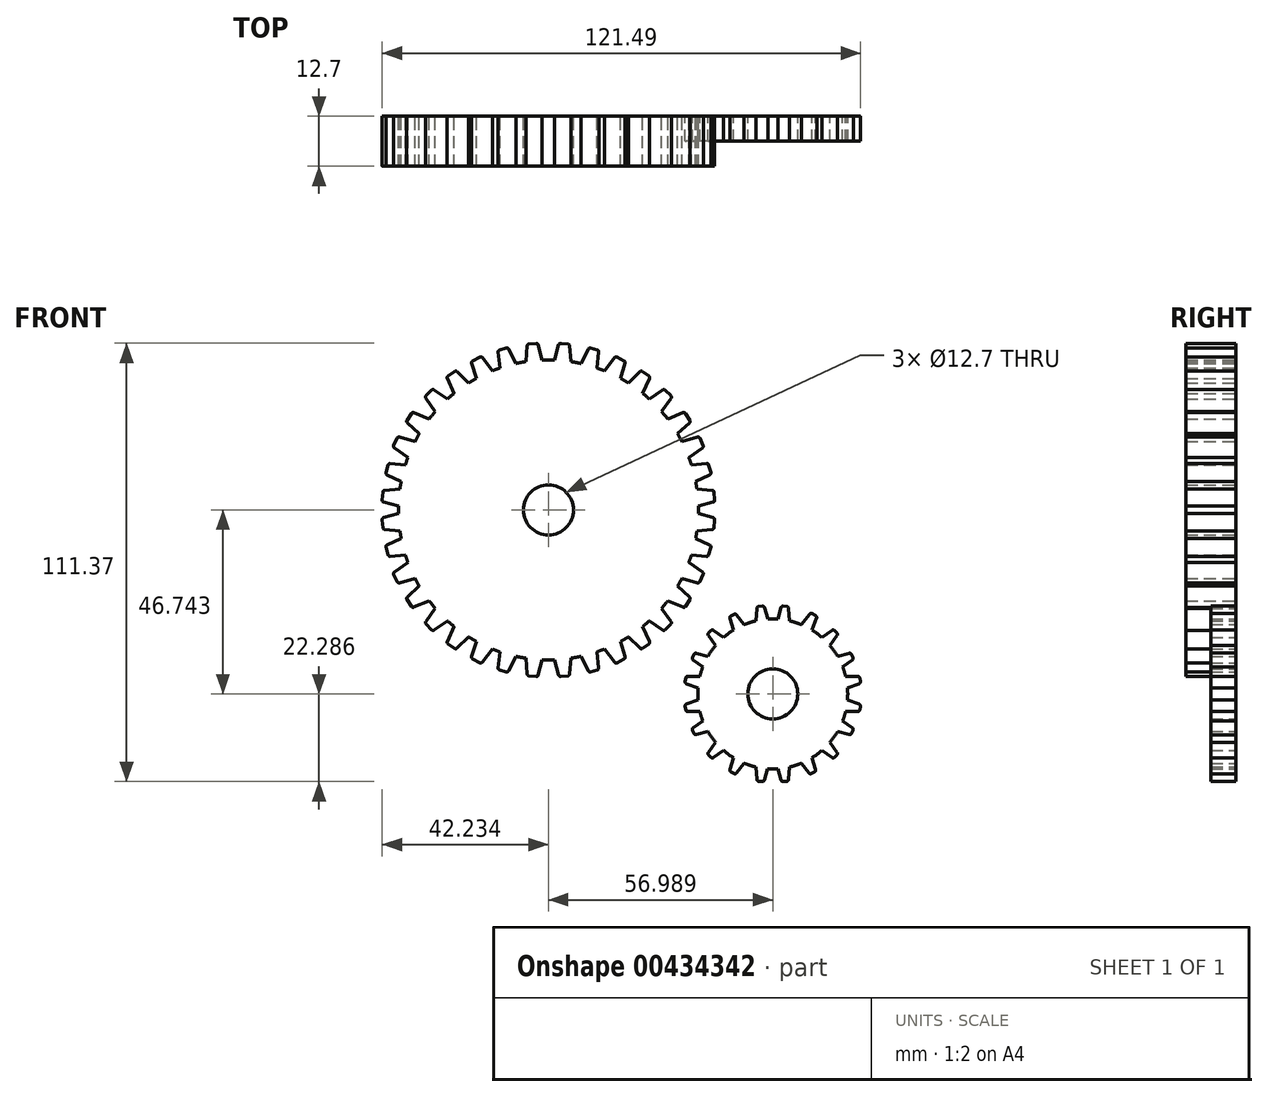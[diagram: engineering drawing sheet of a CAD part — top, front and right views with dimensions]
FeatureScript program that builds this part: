
annotation { "Feature Type Name" : "Feature", "Feature Type Description" : "" }
export const myFeature = defineFeature(function(context is Context, id is Id, definition is map)
    precondition{}
    {
        {
            var Q0;
            Q0=qCreatedBy(makeId("Front.planeOp"),FACE);
            var sketch = newSketch(context, id + "F0", { "sketchPlane" : qUnion([Q0])});
            skCircle(sketch, "E0", {"center": v(-12.13, 9.66) * mm, "radius": 38.1 * mm});
            skCircle(sketch, "E1", {"center": v(-12.13, 9.66) * mm, "radius": 6.35 * mm});
            skLineSegment(sketch, "E2", {"start": v(-6.7, 44.55) * mm, "end": v(-10.75, 44.9) * mm});
            skLineSegment(sketch, "E3", {"start": v(-11.15, 45.49) * mm, "end": v(-9.51, 51.62) * mm});
            skLineSegment(sketch, "E4", {"start": v(-8.98, 52) * mm, "end": v(-7.2, 51.84) * mm});
            skLineSegment(sketch, "E5", {"start": v(-6.75, 51.38) * mm, "end": v(-6.2, 45.05) * mm});
            skPoint(sketch, "E6.visualSharp", {"position": v(-6.78, 51.8) * mm});
            skPoint(sketch, "E7.visualSharp", {"position": v(-9.4, 52.03) * mm});
            skArc(sketch, "E7.filletArc", {"start": v(-8.98, 52) * mm, "mid": v(-9.31, 51.9) * mm, "end": v(-9.51, 51.62) * mm});
            skPoint(sketch, "E8.visualSharp", {"position": v(-6.15, 44.5) * mm});
            skArc(sketch, "E8.filletArc", {"start": v(-6.7, 44.55) * mm, "mid": v(-6.33, 44.68) * mm, "end": v(-6.2, 45.05) * mm});
            skPoint(sketch, "E9.visualSharp", {"position": v(-11.3, 44.95) * mm});
            skArc(sketch, "E9.filletArc", {"start": v(-11.15, 45.49) * mm, "mid": v(-11.09, 45.1) * mm, "end": v(-10.75, 44.9) * mm});
            skArc(sketch, "E10.filletArc", {"start": v(-6.75, 51.38) * mm, "mid": v(-6.9, 51.7) * mm, "end": v(-7.2, 51.84) * mm});
            skLineSegment(sketch, "E11", {"start": v(-12.13, -28.44) * mm, "end": v(-12.13, 47.76) * mm, "construction": true});
            skLineSegment(sketch, "E12", {"start": v(-50.23, 9.66) * mm, "end": v(25.97, 9.66) * mm, "construction": true});
            skLineSegment(sketch, "E13", {"start": v(-0.73, 43.06) * mm, "end": v(-4.62, 44.26) * mm});
            skLineSegment(sketch, "E14", {"start": v(-4.9, 44.92) * mm, "end": v(-2, 50.57) * mm});
            skLineSegment(sketch, "E15", {"start": v(-1.4, 50.82) * mm, "end": v(0.3, 50.3) * mm});
            skLineSegment(sketch, "E16", {"start": v(0.66, 49.75) * mm, "end": v(-0.13, 43.45) * mm});
            skPoint(sketch, "E17.visualSharp", {"position": v(1, 48.98) * mm});
            skPoint(sketch, "E18.visualSharp", {"position": v(-1.8, 50.94) * mm});
            skArc(sketch, "E18.filletArc", {"start": v(-1.4, 50.82) * mm, "mid": v(-1.74, 50.8) * mm, "end": v(-2, 50.57) * mm});
            skPoint(sketch, "E19.visualSharp", {"position": v(-0.2, 42.9) * mm});
            skArc(sketch, "E19.filletArc", {"start": v(-0.73, 43.06) * mm, "mid": v(-0.34, 43.11) * mm, "end": v(-0.13, 43.45) * mm});
            skPoint(sketch, "E20.visualSharp", {"position": v(-5.14, 44.42) * mm});
            skArc(sketch, "E20.filletArc", {"start": v(-4.9, 44.92) * mm, "mid": v(-4.9, 44.52) * mm, "end": v(-4.62, 44.26) * mm});
            skArc(sketch, "E21.filletArc", {"start": v(0.66, 49.75) * mm, "mid": v(0.58, 50.09) * mm, "end": v(0.3, 50.3) * mm});
            skLineSegment(sketch, "E22", {"start": v(4.8, 40.61) * mm, "end": v(0.96, 42.6) * mm});
            skLineSegment(sketch, "E23", {"start": v(0.8, 43.3) * mm, "end": v(4.66, 48.34) * mm});
            skLineSegment(sketch, "E24", {"start": v(5.3, 48.48) * mm, "end": v(7.1, 47.55) * mm});
            skLineSegment(sketch, "E25", {"start": v(7.36, 46.94) * mm, "end": v(5.45, 40.88) * mm});
            skPoint(sketch, "E26.visualSharp", {"position": v(7.48, 47.35) * mm});
            skPoint(sketch, "E27.visualSharp", {"position": v(4.92, 48.68) * mm});
            skArc(sketch, "E27.filletArc", {"start": v(5.3, 48.48) * mm, "mid": v(4.96, 48.53) * mm, "end": v(4.66, 48.34) * mm});
            skPoint(sketch, "E28.visualSharp", {"position": v(5.29, 40.36) * mm});
            skArc(sketch, "E28.filletArc", {"start": v(4.8, 40.61) * mm, "mid": v(5.19, 40.6) * mm, "end": v(5.45, 40.88) * mm});
            skPoint(sketch, "E29.visualSharp", {"position": v(0.47, 42.86) * mm});
            skArc(sketch, "E29.filletArc", {"start": v(0.8, 43.3) * mm, "mid": v(0.72, 42.91) * mm, "end": v(0.96, 42.6) * mm});
            skArc(sketch, "E30.filletArc", {"start": v(7.36, 46.94) * mm, "mid": v(7.34, 47.3) * mm, "end": v(7.1, 47.55) * mm});
            skLineSegment(sketch, "E31", {"start": v(10.2, 37.1) * mm, "end": v(6.65, 39.59) * mm});
            skLineSegment(sketch, "E32", {"start": v(6.59, 40.3) * mm, "end": v(11.08, 44.78) * mm});
            skLineSegment(sketch, "E33", {"start": v(11.73, 44.84) * mm, "end": v(13.4, 43.67) * mm});
            skLineSegment(sketch, "E34", {"start": v(13.56, 43.04) * mm, "end": v(10.88, 37.29) * mm});
            skPoint(sketch, "E35.visualSharp", {"position": v(13.74, 43.43) * mm});
            skPoint(sketch, "E36.visualSharp", {"position": v(11.38, 45.08) * mm});
            skArc(sketch, "E36.filletArc", {"start": v(11.73, 44.84) * mm, "mid": v(11.4, 44.93) * mm, "end": v(11.08, 44.78) * mm});
            skPoint(sketch, "E37.visualSharp", {"position": v(10.64, 36.79) * mm});
            skArc(sketch, "E37.filletArc", {"start": v(10.2, 37.1) * mm, "mid": v(10.58, 37.04) * mm, "end": v(10.88, 37.29) * mm});
            skPoint(sketch, "E38.visualSharp", {"position": v(6.2, 39.9) * mm});
            skArc(sketch, "E38.filletArc", {"start": v(6.59, 40.3) * mm, "mid": v(6.45, 39.92) * mm, "end": v(6.65, 39.59) * mm});
            skArc(sketch, "E39.filletArc", {"start": v(13.56, 43.04) * mm, "mid": v(13.6, 43.39) * mm, "end": v(13.4, 43.67) * mm});
            skLineSegment(sketch, "E40", {"start": v(14.66, 32.76) * mm, "end": v(11.6, 35.83) * mm});
            skLineSegment(sketch, "E41", {"start": v(11.67, 36.54) * mm, "end": v(16.88, 40.17) * mm});
            skLineSegment(sketch, "E42", {"start": v(17.53, 40.1) * mm, "end": v(18.97, 38.67) * mm});
            skLineSegment(sketch, "E43", {"start": v(19.02, 38.02) * mm, "end": v(15.36, 32.82) * mm});
            skPoint(sketch, "E44.visualSharp", {"position": v(19.27, 38.36) * mm});
            skPoint(sketch, "E45.visualSharp", {"position": v(17.23, 40.41) * mm});
            skArc(sketch, "E45.filletArc", {"start": v(17.53, 40.1) * mm, "mid": v(17.22, 40.26) * mm, "end": v(16.88, 40.17) * mm});
            skPoint(sketch, "E46.visualSharp", {"position": v(15.05, 32.37) * mm});
            skArc(sketch, "E46.filletArc", {"start": v(14.66, 32.76) * mm, "mid": v(15.02, 32.63) * mm, "end": v(15.36, 32.82) * mm});
            skPoint(sketch, "E47.visualSharp", {"position": v(11.22, 36.22) * mm});
            skArc(sketch, "E47.filletArc", {"start": v(11.67, 36.54) * mm, "mid": v(11.47, 36.2) * mm, "end": v(11.6, 35.83) * mm});
            skArc(sketch, "E48.filletArc", {"start": v(19.02, 38.02) * mm, "mid": v(19.11, 38.35) * mm, "end": v(18.97, 38.67) * mm});
            skLineSegment(sketch, "E49", {"start": v(18.32, 27.6) * mm, "end": v(16, 31.25) * mm});
            skLineSegment(sketch, "E50", {"start": v(16.22, 31.92) * mm, "end": v(22.08, 34.35) * mm});
            skLineSegment(sketch, "E51", {"start": v(22.7, 34.15) * mm, "end": v(23.8, 32.44) * mm});
            skLineSegment(sketch, "E52", {"start": v(23.71, 31.8) * mm, "end": v(19.03, 27.5) * mm});
            skPoint(sketch, "E53.visualSharp", {"position": v(24.03, 32.08) * mm});
            skPoint(sketch, "E54.visualSharp", {"position": v(22.48, 34.51) * mm});
            skArc(sketch, "E54.filletArc", {"start": v(22.7, 34.15) * mm, "mid": v(22.43, 34.37) * mm, "end": v(22.08, 34.35) * mm});
            skPoint(sketch, "E55.visualSharp", {"position": v(18.62, 27.13) * mm});
            skArc(sketch, "E55.filletArc", {"start": v(18.32, 27.6) * mm, "mid": v(18.65, 27.39) * mm, "end": v(19.03, 27.5) * mm});
            skPoint(sketch, "E56.visualSharp", {"position": v(15.7, 31.71) * mm});
            skArc(sketch, "E56.filletArc", {"start": v(16.22, 31.92) * mm, "mid": v(15.95, 31.64) * mm, "end": v(16, 31.25) * mm});
            skArc(sketch, "E57.filletArc", {"start": v(23.71, 31.8) * mm, "mid": v(23.87, 32.1) * mm, "end": v(23.8, 32.44) * mm});
            skLineSegment(sketch, "E58", {"start": v(21.12, 21.96) * mm, "end": v(19.29, 25.88) * mm});
            skLineSegment(sketch, "E59", {"start": v(19.6, 26.52) * mm, "end": v(25.72, 28.16) * mm});
            skLineSegment(sketch, "E60", {"start": v(26.32, 27.89) * mm, "end": v(27.17, 26.04) * mm});
            skLineSegment(sketch, "E61", {"start": v(27, 25.41) * mm, "end": v(21.8, 21.77) * mm});
            skPoint(sketch, "E62.visualSharp", {"position": v(27.35, 25.66) * mm});
            skPoint(sketch, "E63.visualSharp", {"position": v(26.14, 28.27) * mm});
            skArc(sketch, "E63.filletArc", {"start": v(26.32, 27.89) * mm, "mid": v(26.07, 28.13) * mm, "end": v(25.72, 28.16) * mm});
            skPoint(sketch, "E64.visualSharp", {"position": v(21.35, 21.45) * mm});
            skArc(sketch, "E64.filletArc", {"start": v(21.12, 21.96) * mm, "mid": v(21.42, 21.7) * mm, "end": v(21.8, 21.77) * mm});
            skPoint(sketch, "E65.visualSharp", {"position": v(19.06, 26.38) * mm});
            skArc(sketch, "E65.filletArc", {"start": v(19.6, 26.52) * mm, "mid": v(19.29, 26.27) * mm, "end": v(19.29, 25.88) * mm});
            skArc(sketch, "E66.filletArc", {"start": v(27, 25.41) * mm, "mid": v(27.2, 25.7) * mm, "end": v(27.17, 26.04) * mm});
            skLineSegment(sketch, "E67", {"start": v(22.38, 16.38) * mm, "end": v(21.39, 20.06) * mm});
            skLineSegment(sketch, "E68", {"start": v(21.98, 20.92) * mm, "end": v(28.05, 21.46) * mm});
            skLineSegment(sketch, "E69", {"start": v(28.59, 21.08) * mm, "end": v(29.12, 19.12) * mm});
            skLineSegment(sketch, "E70", {"start": v(28.84, 18.53) * mm, "end": v(23.32, 15.95) * mm});
            skPoint(sketch, "E71.visualSharp", {"position": v(29.23, 18.71) * mm});
            skPoint(sketch, "E72.visualSharp", {"position": v(28.48, 21.5) * mm});
            skArc(sketch, "E72.filletArc", {"start": v(28.59, 21.08) * mm, "mid": v(28.39, 21.37) * mm, "end": v(28.05, 21.46) * mm});
            skPoint(sketch, "E73.visualSharp", {"position": v(22.6, 15.6) * mm});
            skArc(sketch, "E73.filletArc", {"start": v(22.38, 16.38) * mm, "mid": v(22.75, 15.95) * mm, "end": v(23.32, 15.95) * mm});
            skPoint(sketch, "E74.visualSharp", {"position": v(21.18, 20.85) * mm});
            skArc(sketch, "E74.filletArc", {"start": v(21.98, 20.92) * mm, "mid": v(21.49, 20.63) * mm, "end": v(21.39, 20.06) * mm});
            skArc(sketch, "E75.filletArc", {"start": v(28.84, 18.53) * mm, "mid": v(29.09, 18.78) * mm, "end": v(29.12, 19.12) * mm});
            skLineSegment(sketch, "E76", {"start": v(23, 10.65) * mm, "end": v(22.66, 14.45) * mm});
            skLineSegment(sketch, "E77", {"start": v(23.4, 15.18) * mm, "end": v(29.47, 14.65) * mm});
            skLineSegment(sketch, "E78", {"start": v(29.93, 14.19) * mm, "end": v(30.1, 12.17) * mm});
            skLineSegment(sketch, "E79", {"start": v(29.73, 11.63) * mm, "end": v(23.85, 10.05) * mm});
            skPoint(sketch, "E80.visualSharp", {"position": v(30.14, 11.74) * mm});
            skPoint(sketch, "E81.visualSharp", {"position": v(29.9, 14.61) * mm});
            skArc(sketch, "E81.filletArc", {"start": v(29.93, 14.19) * mm, "mid": v(29.78, 14.5) * mm, "end": v(29.47, 14.65) * mm});
            skPoint(sketch, "E82.visualSharp", {"position": v(23.06, 9.84) * mm});
            skArc(sketch, "E82.filletArc", {"start": v(23, 10.65) * mm, "mid": v(23.28, 10.15) * mm, "end": v(23.85, 10.05) * mm});
            skPoint(sketch, "E83.visualSharp", {"position": v(22.6, 15.25) * mm});
            skArc(sketch, "E83.filletArc", {"start": v(23.4, 15.18) * mm, "mid": v(22.86, 14.99) * mm, "end": v(22.66, 14.45) * mm});
            skArc(sketch, "E84.filletArc", {"start": v(29.73, 11.63) * mm, "mid": v(30.02, 11.83) * mm, "end": v(30.1, 12.17) * mm});
            skArc(sketch, "E85.MirrorCS", {"start": v(-24.9, 49.75) * mm, "mid": v(-24.83, 50.09) * mm, "end": v(-24.55, 50.3) * mm});
            skArc(sketch, "E86.MirrorCS", {"start": v(-47.96, 31.8) * mm, "mid": v(-48.12, 32.1) * mm, "end": v(-48.05, 32.44) * mm});
            skArc(sketch, "E87.MirrorCS", {"start": v(-37.81, 43.04) * mm, "mid": v(-37.84, 43.39) * mm, "end": v(-37.64, 43.67) * mm});
            skArc(sketch, "E88.MirrorCS", {"start": v(-43.27, 38.02) * mm, "mid": v(-43.36, 38.35) * mm, "end": v(-43.22, 38.67) * mm});
            skArc(sketch, "E89.MirrorCS", {"start": v(-31.6, 46.94) * mm, "mid": v(-31.6, 47.3) * mm, "end": v(-31.36, 47.55) * mm});
            skArc(sketch, "E90.MirrorCS", {"start": v(-19.36, 44.92) * mm, "mid": v(-19.34, 44.52) * mm, "end": v(-19.63, 44.26) * mm});
            skArc(sketch, "E91.MirrorCS", {"start": v(-53.98, 11.63) * mm, "mid": v(-54.27, 11.83) * mm, "end": v(-54.36, 12.17) * mm});
            skLineSegment(sketch, "E92.MirrorCS", {"start": v(-46.96, 34.15) * mm, "end": v(-48.05, 32.44) * mm});
            skLineSegment(sketch, "E93.MirrorCS", {"start": v(-35.98, 44.84) * mm, "end": v(-37.64, 43.67) * mm});
            skLineSegment(sketch, "E94.MirrorCS", {"start": v(-22.86, 50.82) * mm, "end": v(-24.55, 50.3) * mm});
            skArc(sketch, "E95.MirrorCS", {"start": v(-17.5, 51.38) * mm, "mid": v(-17.36, 51.7) * mm, "end": v(-17.04, 51.84) * mm});
            skLineSegment(sketch, "E96.MirrorCS", {"start": v(-41.78, 40.1) * mm, "end": v(-43.22, 38.67) * mm});
            skLineSegment(sketch, "E97.MirrorCS", {"start": v(-29.55, 48.48) * mm, "end": v(-31.36, 47.55) * mm});
            skArc(sketch, "E98.MirrorCS", {"start": v(-22.86, 50.82) * mm, "mid": v(-22.51, 50.8) * mm, "end": v(-22.26, 50.57) * mm});
            skArc(sketch, "E99.MirrorCS", {"start": v(-46.96, 34.15) * mm, "mid": v(-46.68, 34.37) * mm, "end": v(-46.34, 34.35) * mm});
            skArc(sketch, "E100.MirrorCS", {"start": v(-35.98, 44.84) * mm, "mid": v(-35.64, 44.93) * mm, "end": v(-35.33, 44.78) * mm});
            skArc(sketch, "E101.MirrorCS", {"start": v(-50.57, 27.89) * mm, "mid": v(-50.32, 28.13) * mm, "end": v(-49.97, 28.16) * mm});
            skArc(sketch, "E102.MirrorCS", {"start": v(-41.78, 40.1) * mm, "mid": v(-41.47, 40.26) * mm, "end": v(-41.13, 40.17) * mm});
            skArc(sketch, "E103.MirrorCS", {"start": v(-29.55, 48.48) * mm, "mid": v(-29.2, 48.53) * mm, "end": v(-28.92, 48.34) * mm});
            skArc(sketch, "E104.MirrorCS", {"start": v(-23.52, 43.06) * mm, "mid": v(-23.9, 43.11) * mm, "end": v(-24.12, 43.45) * mm});
            skArc(sketch, "E105.MirrorCS", {"start": v(-29.05, 40.61) * mm, "mid": v(-29.44, 40.6) * mm, "end": v(-29.7, 40.88) * mm});
            skArc(sketch, "E106.MirrorCS", {"start": v(-47.24, 10.65) * mm, "mid": v(-47.53, 10.15) * mm, "end": v(-48.1, 10.05) * mm});
            skArc(sketch, "E107.MirrorCS", {"start": v(-30.84, 40.3) * mm, "mid": v(-30.7, 39.92) * mm, "end": v(-30.9, 39.59) * mm});
            skArc(sketch, "E108.MirrorCS", {"start": v(-43.84, 26.52) * mm, "mid": v(-43.54, 26.27) * mm, "end": v(-43.54, 25.88) * mm});
            skArc(sketch, "E109.MirrorCS", {"start": v(-35.92, 36.54) * mm, "mid": v(-35.72, 36.2) * mm, "end": v(-35.86, 35.83) * mm});
            skArc(sketch, "E110.MirrorCS", {"start": v(-25.06, 43.3) * mm, "mid": v(-24.97, 42.91) * mm, "end": v(-25.21, 42.6) * mm});
            skArc(sketch, "E111.MirrorCS", {"start": v(-47.65, 15.18) * mm, "mid": v(-47.1, 14.99) * mm, "end": v(-46.91, 14.45) * mm});
            skArc(sketch, "E112.MirrorCS", {"start": v(-53.1, 18.53) * mm, "mid": v(-53.34, 18.78) * mm, "end": v(-53.37, 19.12) * mm});
            skArc(sketch, "E113.MirrorCS", {"start": v(-51.26, 25.41) * mm, "mid": v(-51.46, 25.7) * mm, "end": v(-51.43, 26.04) * mm});
            skLineSegment(sketch, "E114.MirrorCS", {"start": v(-52.84, 21.08) * mm, "end": v(-53.37, 19.12) * mm});
            skLineSegment(sketch, "E115.MirrorCS", {"start": v(-23.52, 43.06) * mm, "end": v(-19.63, 44.26) * mm});
            skLineSegment(sketch, "E116.MirrorCS", {"start": v(-17.56, 44.55) * mm, "end": v(-13.5, 44.9) * mm});
            skLineSegment(sketch, "E117.MirrorCS", {"start": v(-15.27, 52) * mm, "end": v(-17.04, 51.84) * mm});
            skArc(sketch, "E118.MirrorCS", {"start": v(-15.27, 52) * mm, "mid": v(-14.94, 51.9) * mm, "end": v(-14.74, 51.62) * mm});
            skArc(sketch, "E119.MirrorCS", {"start": v(-17.56, 44.55) * mm, "mid": v(-17.92, 44.68) * mm, "end": v(-18.06, 45.05) * mm});
            skArc(sketch, "E120.MirrorCS", {"start": v(-13.1, 45.49) * mm, "mid": v(-13.16, 45.1) * mm, "end": v(-13.5, 44.9) * mm});
            skLineSegment(sketch, "E121.MirrorCS", {"start": v(-50.57, 27.89) * mm, "end": v(-51.43, 26.04) * mm});
            skLineSegment(sketch, "E122.MirrorCS", {"start": v(-54.18, 14.19) * mm, "end": v(-54.36, 12.17) * mm});
            skArc(sketch, "E123.MirrorCS", {"start": v(-52.84, 21.08) * mm, "mid": v(-52.64, 21.37) * mm, "end": v(-52.3, 21.46) * mm});
            skArc(sketch, "E124.MirrorCS", {"start": v(-54.18, 14.19) * mm, "mid": v(-54.03, 14.5) * mm, "end": v(-53.72, 14.65) * mm});
            skArc(sketch, "E125.MirrorCS", {"start": v(-34.44, 37.1) * mm, "mid": v(-34.83, 37.04) * mm, "end": v(-35.13, 37.29) * mm});
            skLineSegment(sketch, "E126.MirrorCS", {"start": v(-42.58, 27.6) * mm, "end": v(-40.25, 31.25) * mm});
            skLineSegment(sketch, "E127.MirrorCS", {"start": v(-47.24, 10.65) * mm, "end": v(-46.91, 14.45) * mm});
            skLineSegment(sketch, "E128.MirrorCS", {"start": v(-45.37, 21.96) * mm, "end": v(-43.54, 25.88) * mm});
            skArc(sketch, "E129.MirrorCS", {"start": v(-46.63, 16.38) * mm, "mid": v(-47, 15.95) * mm, "end": v(-47.58, 15.95) * mm});
            skArc(sketch, "E130.MirrorCS", {"start": v(-42.58, 27.6) * mm, "mid": v(-42.9, 27.39) * mm, "end": v(-43.28, 27.5) * mm});
            skArc(sketch, "E131.MirrorCS", {"start": v(-38.9, 32.76) * mm, "mid": v(-39.27, 32.63) * mm, "end": v(-39.61, 32.82) * mm});
            skArc(sketch, "E132.MirrorCS", {"start": v(-45.37, 21.96) * mm, "mid": v(-45.67, 21.7) * mm, "end": v(-46.05, 21.77) * mm});
            skArc(sketch, "E133.MirrorCS", {"start": v(-46.24, 20.92) * mm, "mid": v(-45.74, 20.63) * mm, "end": v(-45.64, 20.06) * mm});
            skArc(sketch, "E134.MirrorCS", {"start": v(-40.47, 31.92) * mm, "mid": v(-40.2, 31.64) * mm, "end": v(-40.25, 31.25) * mm});
            skLineSegment(sketch, "E135.MirrorCS", {"start": v(-46.63, 16.38) * mm, "end": v(-45.64, 20.06) * mm});
            skLineSegment(sketch, "E136.MirrorCS", {"start": v(-34.44, 37.1) * mm, "end": v(-30.9, 39.59) * mm});
            skLineSegment(sketch, "E137.MirrorCS", {"start": v(-29.05, 40.61) * mm, "end": v(-25.21, 42.6) * mm});
            skLineSegment(sketch, "E138.MirrorCS", {"start": v(-38.9, 32.76) * mm, "end": v(-35.86, 35.83) * mm});
            skPoint(sketch, "E139.MirrorP", {"position": v(-48.28, 32.08) * mm});
            skPoint(sketch, "E140.MirrorP", {"position": v(-17.47, 51.8) * mm});
            skPoint(sketch, "E141.MirrorP", {"position": v(-53.48, 18.71) * mm});
            skPoint(sketch, "E142.MirrorP", {"position": v(-51.6, 25.66) * mm});
            skPoint(sketch, "E143.MirrorP", {"position": v(-43.52, 38.36) * mm});
            skPoint(sketch, "E144.MirrorP", {"position": v(-54.4, 11.74) * mm});
            skPoint(sketch, "E145.MirrorP", {"position": v(-25.24, 48.98) * mm});
            skPoint(sketch, "E146.MirrorP", {"position": v(-31.73, 47.35) * mm});
            skPoint(sketch, "E147.MirrorP", {"position": v(-38, 43.43) * mm});
            skPoint(sketch, "E148.MirrorP", {"position": v(-24.05, 42.9) * mm});
            skPoint(sketch, "E149.MirrorP", {"position": v(-35.63, 45.08) * mm});
            skPoint(sketch, "E150.MirrorP", {"position": v(-29.17, 48.68) * mm});
            skPoint(sketch, "E151.MirrorP", {"position": v(-46.84, 15.25) * mm});
            skPoint(sketch, "E152.MirrorP", {"position": v(-12.95, 44.95) * mm});
            skPoint(sketch, "E153.MirrorP", {"position": v(-45.43, 20.85) * mm});
            skPoint(sketch, "E154.MirrorP", {"position": v(-39.3, 32.37) * mm});
            skPoint(sketch, "E155.MirrorP", {"position": v(-46.73, 34.51) * mm});
            skPoint(sketch, "E156.MirrorP", {"position": v(-34.9, 36.79) * mm});
            skPoint(sketch, "E157.MirrorP", {"position": v(-24.72, 42.86) * mm});
            skPoint(sketch, "E158.MirrorP", {"position": v(-19.1, 44.42) * mm});
            skPoint(sketch, "E159.MirrorP", {"position": v(-50.39, 28.27) * mm});
            skLineSegment(sketch, "E160.MirrorCS", {"start": v(-46.24, 20.92) * mm, "end": v(-52.3, 21.46) * mm});
            skLineSegment(sketch, "E161.MirrorCS", {"start": v(-40.47, 31.92) * mm, "end": v(-46.34, 34.35) * mm});
            skLineSegment(sketch, "E162.MirrorCS", {"start": v(-30.84, 40.3) * mm, "end": v(-35.33, 44.78) * mm});
            skPoint(sketch, "E163.MirrorP", {"position": v(-29.54, 40.36) * mm});
            skPoint(sketch, "E164.MirrorP", {"position": v(-41.48, 40.41) * mm});
            skLineSegment(sketch, "E165.MirrorCS", {"start": v(-25.06, 43.3) * mm, "end": v(-28.92, 48.34) * mm});
            skLineSegment(sketch, "E166.MirrorCS", {"start": v(-47.65, 15.18) * mm, "end": v(-53.72, 14.65) * mm});
            skLineSegment(sketch, "E167.MirrorCS", {"start": v(-43.84, 26.52) * mm, "end": v(-49.97, 28.16) * mm});
            skLineSegment(sketch, "E168.MirrorCS", {"start": v(-35.92, 36.54) * mm, "end": v(-41.13, 40.17) * mm});
            skLineSegment(sketch, "E169.MirrorCS", {"start": v(-19.36, 44.92) * mm, "end": v(-22.26, 50.57) * mm});
            skLineSegment(sketch, "E170.MirrorCS", {"start": v(-13.1, 45.49) * mm, "end": v(-14.74, 51.62) * mm});
            skLineSegment(sketch, "E171.MirrorCS", {"start": v(-17.5, 51.38) * mm, "end": v(-18.06, 45.05) * mm});
            skPoint(sketch, "E172.MirrorP", {"position": v(-14.85, 52.03) * mm});
            skPoint(sketch, "E173.MirrorP", {"position": v(-52.73, 21.5) * mm});
            skPoint(sketch, "E174.MirrorP", {"position": v(-30.45, 39.9) * mm});
            skPoint(sketch, "E175.MirrorP", {"position": v(-42.87, 27.13) * mm});
            skPoint(sketch, "E176.MirrorP", {"position": v(-35.47, 36.22) * mm});
            skPoint(sketch, "E177.MirrorP", {"position": v(-54.14, 14.61) * mm});
            skPoint(sketch, "E178.MirrorP", {"position": v(-45.6, 21.45) * mm});
            skLineSegment(sketch, "E179.MirrorCS", {"start": v(-24.9, 49.75) * mm, "end": v(-24.12, 43.45) * mm});
            skLineSegment(sketch, "E180.MirrorCS", {"start": v(-53.1, 18.53) * mm, "end": v(-47.58, 15.95) * mm});
            skLineSegment(sketch, "E181.MirrorCS", {"start": v(-47.96, 31.8) * mm, "end": v(-43.28, 27.5) * mm});
            skLineSegment(sketch, "E182.MirrorCS", {"start": v(-37.81, 43.04) * mm, "end": v(-35.13, 37.29) * mm});
            skLineSegment(sketch, "E183.MirrorCS", {"start": v(-51.26, 25.41) * mm, "end": v(-46.05, 21.77) * mm});
            skLineSegment(sketch, "E184.MirrorCS", {"start": v(-43.27, 38.02) * mm, "end": v(-39.61, 32.82) * mm});
            skLineSegment(sketch, "E185.MirrorCS", {"start": v(-53.98, 11.63) * mm, "end": v(-48.1, 10.05) * mm});
            skLineSegment(sketch, "E186.MirrorCS", {"start": v(-31.6, 46.94) * mm, "end": v(-29.7, 40.88) * mm});
            skPoint(sketch, "E187.MirrorP", {"position": v(-22.45, 50.94) * mm});
            skPoint(sketch, "E188.MirrorP", {"position": v(-47.31, 9.84) * mm});
            skPoint(sketch, "E189.MirrorP", {"position": v(-43.3, 26.38) * mm});
            skPoint(sketch, "E190.MirrorP", {"position": v(-18.1, 44.5) * mm});
            skPoint(sketch, "E191.MirrorP", {"position": v(-46.84, 15.6) * mm});
            skPoint(sketch, "E192.MirrorP", {"position": v(-39.96, 31.71) * mm});
            skArc(sketch, "E193.MirrorCS", {"start": v(-17.5, -32.06) * mm, "mid": v(-17.36, -32.38) * mm, "end": v(-17.04, -32.52) * mm});
            skArc(sketch, "E194.MirrorCS", {"start": v(-35.92, -17.22) * mm, "mid": v(-35.72, -16.88) * mm, "end": v(-35.86, -16.51) * mm});
            skArc(sketch, "E195.MirrorCS", {"start": v(-34.44, -17.79) * mm, "mid": v(-34.83, -17.72) * mm, "end": v(-35.13, -17.97) * mm});
            skArc(sketch, "E196.MirrorCS", {"start": v(-54.18, 5.13) * mm, "mid": v(-54.03, 4.81) * mm, "end": v(-53.72, 4.67) * mm});
            skArc(sketch, "E197.MirrorCS", {"start": v(0.66, -30.43) * mm, "mid": v(0.58, -30.77) * mm, "end": v(0.3, -30.98) * mm});
            skArc(sketch, "E198.MirrorCS", {"start": v(-46.63, 2.93) * mm, "mid": v(-47, 3.37) * mm, "end": v(-47.58, 3.37) * mm});
            skArc(sketch, "E199.MirrorCS", {"start": v(-52.84, -1.77) * mm, "mid": v(-52.64, -2.05) * mm, "end": v(-52.3, -2.14) * mm});
            skArc(sketch, "E200.MirrorCS", {"start": v(-53.1, 0.79) * mm, "mid": v(-53.34, 0.54) * mm, "end": v(-53.37, 0.2) * mm});
            skLineSegment(sketch, "E201.MirrorCS", {"start": v(-47.65, 4.14) * mm, "end": v(-53.72, 4.67) * mm});
            skArc(sketch, "E202.MirrorCS", {"start": v(-47.65, 4.14) * mm, "mid": v(-47.1, 4.33) * mm, "end": v(-46.91, 4.87) * mm});
            skLineSegment(sketch, "E203.MirrorCS", {"start": v(5.3, -29.16) * mm, "end": v(7.1, -28.23) * mm});
            skLineSegment(sketch, "E204.MirrorCS", {"start": v(26.32, -8.57) * mm, "end": v(27.17, -6.73) * mm});
            skLineSegment(sketch, "E205.MirrorCS", {"start": v(0.8, -23.98) * mm, "end": v(4.66, -29.02) * mm});
            skArc(sketch, "E206.MirrorCS", {"start": v(23, 8.67) * mm, "mid": v(23.28, 9.16) * mm, "end": v(23.85, 9.26) * mm});
            skLineSegment(sketch, "E207.MirrorCS", {"start": v(-52.84, -1.77) * mm, "end": v(-53.37, 0.2) * mm});
            skArc(sketch, "E208.MirrorCS", {"start": v(21.12, -2.64) * mm, "mid": v(21.42, -2.39) * mm, "end": v(21.8, -2.45) * mm});
            skLineSegment(sketch, "E209.MirrorCS", {"start": v(21.12, -2.64) * mm, "end": v(19.29, -6.56) * mm});
            skLineSegment(sketch, "E210.MirrorCS", {"start": v(-35.98, -25.52) * mm, "end": v(-37.64, -24.36) * mm});
            skLineSegment(sketch, "E211.MirrorCS", {"start": v(-35.92, -17.22) * mm, "end": v(-41.13, -20.85) * mm});
            skArc(sketch, "E212.MirrorCS", {"start": v(13.56, -23.73) * mm, "mid": v(13.6, -24.07) * mm, "end": v(13.4, -24.36) * mm});
            skArc(sketch, "E213.MirrorCS", {"start": v(23.71, -12.47) * mm, "mid": v(23.87, -12.78) * mm, "end": v(23.8, -13.12) * mm});
            skArc(sketch, "E214.MirrorCS", {"start": v(28.84, 0.79) * mm, "mid": v(29.09, 0.54) * mm, "end": v(29.12, 0.2) * mm});
            skArc(sketch, "E215.MirrorCS", {"start": v(-51.26, -6.1) * mm, "mid": v(-51.46, -6.38) * mm, "end": v(-51.43, -6.73) * mm});
            skArc(sketch, "E216.MirrorCS", {"start": v(5.3, -29.16) * mm, "mid": v(4.96, -29.2) * mm, "end": v(4.66, -29.02) * mm});
            skArc(sketch, "E217.MirrorCS", {"start": v(26.32, -8.57) * mm, "mid": v(26.07, -8.81) * mm, "end": v(25.72, -8.84) * mm});
            skLineSegment(sketch, "E218.MirrorCS", {"start": v(-46.24, -1.6) * mm, "end": v(-52.3, -2.14) * mm});
            skArc(sketch, "E219.MirrorCS", {"start": v(21.98, -1.6) * mm, "mid": v(21.49, -1.31) * mm, "end": v(21.39, -0.75) * mm});
            skArc(sketch, "E220.MirrorCS", {"start": v(-53.98, 7.69) * mm, "mid": v(-54.27, 7.49) * mm, "end": v(-54.36, 7.15) * mm});
            skArc(sketch, "E221.MirrorCS", {"start": v(-4.9, -25.6) * mm, "mid": v(-4.9, -25.2) * mm, "end": v(-4.62, -24.94) * mm});
            skLineSegment(sketch, "E222.MirrorCS", {"start": v(29.73, 7.69) * mm, "end": v(23.85, 9.26) * mm});
            skLineSegment(sketch, "E223.MirrorCS", {"start": v(-41.78, -20.8) * mm, "end": v(-43.22, -19.35) * mm});
            skLineSegment(sketch, "E224.MirrorCS", {"start": v(27, -6.1) * mm, "end": v(21.8, -2.45) * mm});
            skArc(sketch, "E225.MirrorCS", {"start": v(-19.36, -25.6) * mm, "mid": v(-19.34, -25.2) * mm, "end": v(-19.63, -24.94) * mm});
            skLineSegment(sketch, "E226.MirrorCS", {"start": v(-54.18, 5.13) * mm, "end": v(-54.36, 7.15) * mm});
            skArc(sketch, "E227.MirrorCS", {"start": v(27, -6.1) * mm, "mid": v(27.2, -6.38) * mm, "end": v(27.17, -6.73) * mm});
            skLineSegment(sketch, "E228.MirrorCS", {"start": v(28.59, -1.77) * mm, "end": v(29.12, 0.2) * mm});
            skLineSegment(sketch, "E229.MirrorCS", {"start": v(11.73, -25.52) * mm, "end": v(13.4, -24.36) * mm});
            skLineSegment(sketch, "E230.MirrorCS", {"start": v(0.66, -30.43) * mm, "end": v(-0.13, -24.13) * mm});
            skLineSegment(sketch, "E231.MirrorCS", {"start": v(-34.44, -17.79) * mm, "end": v(-30.9, -20.27) * mm});
            skArc(sketch, "E232.MirrorCS", {"start": v(-0.73, -23.74) * mm, "mid": v(-0.34, -23.8) * mm, "end": v(-0.13, -24.13) * mm});
            skArc(sketch, "E233.MirrorCS", {"start": v(-1.4, -31.5) * mm, "mid": v(-1.74, -31.48) * mm, "end": v(-2, -31.25) * mm});
            skArc(sketch, "E234.MirrorCS", {"start": v(11.73, -25.52) * mm, "mid": v(11.4, -25.61) * mm, "end": v(11.08, -25.47) * mm});
            skLineSegment(sketch, "E235.MirrorCS", {"start": v(-23.52, -23.74) * mm, "end": v(-19.63, -24.94) * mm});
            skArc(sketch, "E236.MirrorCS", {"start": v(0.8, -23.98) * mm, "mid": v(0.72, -23.6) * mm, "end": v(0.96, -23.29) * mm});
            skLineSegment(sketch, "E237.MirrorCS", {"start": v(-15.27, -32.68) * mm, "end": v(-17.04, -32.52) * mm});
            skLineSegment(sketch, "E238.MirrorCS", {"start": v(-37.81, -23.73) * mm, "end": v(-35.13, -17.97) * mm});
            skArc(sketch, "E239.MirrorCS", {"start": v(7.36, -27.63) * mm, "mid": v(7.34, -27.97) * mm, "end": v(7.1, -28.23) * mm});
            skArc(sketch, "E240.MirrorCS", {"start": v(-41.78, -20.8) * mm, "mid": v(-41.47, -20.94) * mm, "end": v(-41.13, -20.85) * mm});
            skArc(sketch, "E241.MirrorCS", {"start": v(-37.81, -23.73) * mm, "mid": v(-37.84, -24.07) * mm, "end": v(-37.64, -24.36) * mm});
            skArc(sketch, "E242.MirrorCS", {"start": v(-43.27, -18.7) * mm, "mid": v(-43.36, -19.03) * mm, "end": v(-43.22, -19.35) * mm});
            skArc(sketch, "E243.MirrorCS", {"start": v(28.59, -1.77) * mm, "mid": v(28.39, -2.05) * mm, "end": v(28.05, -2.14) * mm});
            skArc(sketch, "E244.MirrorCS", {"start": v(-45.37, -2.64) * mm, "mid": v(-45.67, -2.39) * mm, "end": v(-46.05, -2.45) * mm});
            skArc(sketch, "E245.MirrorCS", {"start": v(-35.98, -25.52) * mm, "mid": v(-35.64, -25.61) * mm, "end": v(-35.33, -25.47) * mm});
            skLineSegment(sketch, "E246.MirrorCS", {"start": v(21.98, -1.6) * mm, "end": v(28.05, -2.14) * mm});
            skArc(sketch, "E247.MirrorCS", {"start": v(-46.24, -1.6) * mm, "mid": v(-45.74, -1.31) * mm, "end": v(-45.64, -0.75) * mm});
            skLineSegment(sketch, "E248.MirrorCS", {"start": v(-17.5, -32.06) * mm, "end": v(-18.06, -25.73) * mm});
            skArc(sketch, "E249.MirrorCS", {"start": v(-50.57, -8.57) * mm, "mid": v(-50.32, -8.81) * mm, "end": v(-49.97, -8.84) * mm});
            skArc(sketch, "E250.MirrorCS", {"start": v(-15.27, -32.68) * mm, "mid": v(-14.94, -32.59) * mm, "end": v(-14.74, -32.3) * mm});
            skArc(sketch, "E251.MirrorCS", {"start": v(-6.75, -32.06) * mm, "mid": v(-6.9, -32.38) * mm, "end": v(-7.2, -32.52) * mm});
            skLineSegment(sketch, "E252.MirrorCS", {"start": v(-53.1, 0.79) * mm, "end": v(-47.58, 3.37) * mm});
            skLineSegment(sketch, "E253.MirrorCS", {"start": v(-46.63, 2.93) * mm, "end": v(-45.64, -0.75) * mm});
            skArc(sketch, "E254.MirrorCS", {"start": v(-17.56, -25.23) * mm, "mid": v(-17.92, -25.37) * mm, "end": v(-18.06, -25.73) * mm});
            skLineSegment(sketch, "E255.MirrorCS", {"start": v(-1.4, -31.5) * mm, "end": v(0.3, -30.98) * mm});
            skLineSegment(sketch, "E256.MirrorCS", {"start": v(-8.98, -32.68) * mm, "end": v(-7.2, -32.52) * mm});
            skArc(sketch, "E257.MirrorCS", {"start": v(-8.98, -32.68) * mm, "mid": v(-9.31, -32.59) * mm, "end": v(-9.51, -32.3) * mm});
            skLineSegment(sketch, "E258.MirrorCS", {"start": v(29.93, 5.13) * mm, "end": v(30.1, 7.15) * mm});
            skArc(sketch, "E259.MirrorCS", {"start": v(-25.06, -23.98) * mm, "mid": v(-24.97, -23.6) * mm, "end": v(-25.21, -23.29) * mm});
            skLineSegment(sketch, "E260.MirrorCS", {"start": v(-42.58, -8.28) * mm, "end": v(-40.25, -11.93) * mm});
            skLineSegment(sketch, "E261.MirrorCS", {"start": v(-25.06, -23.98) * mm, "end": v(-28.92, -29.02) * mm});
            skLineSegment(sketch, "E262.MirrorCS", {"start": v(23.4, 4.14) * mm, "end": v(29.47, 4.67) * mm});
            skArc(sketch, "E263.MirrorCS", {"start": v(-22.86, -31.5) * mm, "mid": v(-22.51, -31.48) * mm, "end": v(-22.26, -31.25) * mm});
            skArc(sketch, "E264.MirrorCS", {"start": v(-42.58, -8.28) * mm, "mid": v(-42.9, -8.07) * mm, "end": v(-43.28, -8.19) * mm});
            skArc(sketch, "E265.MirrorCS", {"start": v(4.8, -21.3) * mm, "mid": v(5.19, -21.28) * mm, "end": v(5.45, -21.57) * mm});
            skLineSegment(sketch, "E266.MirrorCS", {"start": v(-30.84, -20.98) * mm, "end": v(-35.33, -25.47) * mm});
            skLineSegment(sketch, "E267.MirrorCS", {"start": v(23, 8.67) * mm, "end": v(22.66, 4.87) * mm});
            skLineSegment(sketch, "E268.MirrorCS", {"start": v(4.8, -21.3) * mm, "end": v(0.96, -23.29) * mm});
            skArc(sketch, "E269.MirrorCS", {"start": v(29.93, 5.13) * mm, "mid": v(29.78, 4.81) * mm, "end": v(29.47, 4.67) * mm});
            skArc(sketch, "E270.MirrorCS", {"start": v(-43.84, -7.2) * mm, "mid": v(-43.54, -6.95) * mm, "end": v(-43.54, -6.56) * mm});
            skLineSegment(sketch, "E271.MirrorCS", {"start": v(-29.55, -29.16) * mm, "end": v(-31.36, -28.23) * mm});
            skArc(sketch, "E272.MirrorCS", {"start": v(-30.84, -20.98) * mm, "mid": v(-30.7, -20.6) * mm, "end": v(-30.9, -20.27) * mm});
            skLineSegment(sketch, "E273.MirrorCS", {"start": v(-43.27, -18.7) * mm, "end": v(-39.61, -13.5) * mm});
            skArc(sketch, "E274.MirrorCS", {"start": v(6.59, -20.98) * mm, "mid": v(6.45, -20.6) * mm, "end": v(6.65, -20.27) * mm});
            skArc(sketch, "E275.MirrorCS", {"start": v(16.22, -12.6) * mm, "mid": v(15.95, -12.32) * mm, "end": v(16, -11.93) * mm});
            skLineSegment(sketch, "E276.MirrorCS", {"start": v(-43.84, -7.2) * mm, "end": v(-49.97, -8.84) * mm});
            skLineSegment(sketch, "E277.MirrorCS", {"start": v(-45.37, -2.64) * mm, "end": v(-43.54, -6.56) * mm});
            skLineSegment(sketch, "E278.MirrorCS", {"start": v(7.36, -27.63) * mm, "end": v(5.45, -21.57) * mm});
            skArc(sketch, "E279.MirrorCS", {"start": v(22.38, 2.93) * mm, "mid": v(22.75, 3.37) * mm, "end": v(23.32, 3.37) * mm});
            skLineSegment(sketch, "E280.MirrorCS", {"start": v(-38.9, -13.45) * mm, "end": v(-35.86, -16.51) * mm});
            skArc(sketch, "E281.MirrorCS", {"start": v(23.4, 4.14) * mm, "mid": v(22.86, 4.33) * mm, "end": v(22.66, 4.87) * mm});
            skLineSegment(sketch, "E282.MirrorCS", {"start": v(28.84, 0.79) * mm, "end": v(23.32, 3.37) * mm});
            skArc(sketch, "E283.MirrorCS", {"start": v(22.7, -14.84) * mm, "mid": v(22.43, -15.05) * mm, "end": v(22.08, -15.03) * mm});
            skArc(sketch, "E284.MirrorCS", {"start": v(-38.9, -13.45) * mm, "mid": v(-39.27, -13.31) * mm, "end": v(-39.61, -13.5) * mm});
            skArc(sketch, "E285.MirrorCS", {"start": v(29.73, 7.69) * mm, "mid": v(30.02, 7.49) * mm, "end": v(30.1, 7.15) * mm});
            skLineSegment(sketch, "E286.MirrorCS", {"start": v(-51.26, -6.1) * mm, "end": v(-46.05, -2.45) * mm});
            skArc(sketch, "E287.MirrorCS", {"start": v(-40.47, -12.6) * mm, "mid": v(-40.2, -12.32) * mm, "end": v(-40.25, -11.93) * mm});
            skArc(sketch, "E288.MirrorCS", {"start": v(-23.52, -23.74) * mm, "mid": v(-23.9, -23.8) * mm, "end": v(-24.12, -24.13) * mm});
            skArc(sketch, "E289.MirrorCS", {"start": v(-31.6, -27.63) * mm, "mid": v(-31.6, -27.97) * mm, "end": v(-31.36, -28.23) * mm});
            skLineSegment(sketch, "E290.MirrorCS", {"start": v(22.38, 2.93) * mm, "end": v(21.39, -0.75) * mm});
            skArc(sketch, "E291.MirrorCS", {"start": v(-24.9, -30.43) * mm, "mid": v(-24.83, -30.77) * mm, "end": v(-24.55, -30.98) * mm});
            skLineSegment(sketch, "E292.MirrorCS", {"start": v(-50.57, -8.57) * mm, "end": v(-51.43, -6.73) * mm});
            skLineSegment(sketch, "E293.MirrorCS", {"start": v(-29.05, -21.3) * mm, "end": v(-25.21, -23.29) * mm});
            skArc(sketch, "E294.MirrorCS", {"start": v(-29.05, -21.3) * mm, "mid": v(-29.44, -21.28) * mm, "end": v(-29.7, -21.57) * mm});
            skLineSegment(sketch, "E295.MirrorCS", {"start": v(22.7, -14.84) * mm, "end": v(23.8, -13.12) * mm});
            skArc(sketch, "E296.MirrorCS", {"start": v(-29.55, -29.16) * mm, "mid": v(-29.2, -29.2) * mm, "end": v(-28.92, -29.02) * mm});
            skLineSegment(sketch, "E297.MirrorCS", {"start": v(-0.73, -23.74) * mm, "end": v(-4.62, -24.94) * mm});
            skLineSegment(sketch, "E298.MirrorCS", {"start": v(-4.9, -25.6) * mm, "end": v(-2, -31.25) * mm});
            skLineSegment(sketch, "E299.MirrorCS", {"start": v(-6.75, -32.06) * mm, "end": v(-6.2, -25.73) * mm});
            skArc(sketch, "E300.MirrorCS", {"start": v(-6.7, -25.23) * mm, "mid": v(-6.33, -25.37) * mm, "end": v(-6.2, -25.73) * mm});
            skLineSegment(sketch, "E301.MirrorCS", {"start": v(-47.24, 8.67) * mm, "end": v(-46.91, 4.87) * mm});
            skLineSegment(sketch, "E302.MirrorCS", {"start": v(17.53, -20.8) * mm, "end": v(18.97, -19.35) * mm});
            skLineSegment(sketch, "E303.MirrorCS", {"start": v(11.67, -17.22) * mm, "end": v(16.88, -20.85) * mm});
            skArc(sketch, "E304.MirrorCS", {"start": v(19.6, -7.2) * mm, "mid": v(19.29, -6.95) * mm, "end": v(19.29, -6.56) * mm});
            skLineSegment(sketch, "E305.MirrorCS", {"start": v(19.6, -7.2) * mm, "end": v(25.72, -8.84) * mm});
            skLineSegment(sketch, "E306.MirrorCS", {"start": v(-22.86, -31.5) * mm, "end": v(-24.55, -30.98) * mm});
            skLineSegment(sketch, "E307.MirrorCS", {"start": v(-19.36, -25.6) * mm, "end": v(-22.26, -31.25) * mm});
            skArc(sketch, "E308.MirrorCS", {"start": v(11.67, -17.22) * mm, "mid": v(11.47, -16.88) * mm, "end": v(11.6, -16.51) * mm});
            skArc(sketch, "E309.MirrorCS", {"start": v(14.66, -13.45) * mm, "mid": v(15.02, -13.31) * mm, "end": v(15.36, -13.5) * mm});
            skLineSegment(sketch, "E310.MirrorCS", {"start": v(-31.6, -27.63) * mm, "end": v(-29.7, -21.57) * mm});
            skLineSegment(sketch, "E311.MirrorCS", {"start": v(14.66, -13.45) * mm, "end": v(11.6, -16.51) * mm});
            skLineSegment(sketch, "E312.MirrorCS", {"start": v(-40.47, -12.6) * mm, "end": v(-46.34, -15.03) * mm});
            skLineSegment(sketch, "E313.MirrorCS", {"start": v(-46.96, -14.84) * mm, "end": v(-48.05, -13.12) * mm});
            skArc(sketch, "E314.MirrorCS", {"start": v(17.53, -20.8) * mm, "mid": v(17.22, -20.94) * mm, "end": v(16.88, -20.85) * mm});
            skLineSegment(sketch, "E315.MirrorCS", {"start": v(19.02, -18.7) * mm, "end": v(15.36, -13.5) * mm});
            skArc(sketch, "E316.MirrorCS", {"start": v(10.2, -17.79) * mm, "mid": v(10.58, -17.72) * mm, "end": v(10.88, -17.97) * mm});
            skArc(sketch, "E317.MirrorCS", {"start": v(-46.96, -14.84) * mm, "mid": v(-46.68, -15.05) * mm, "end": v(-46.34, -15.03) * mm});
            skArc(sketch, "E318.MirrorCS", {"start": v(19.02, -18.7) * mm, "mid": v(19.11, -19.03) * mm, "end": v(18.97, -19.35) * mm});
            skLineSegment(sketch, "E319.MirrorCS", {"start": v(23.71, -12.47) * mm, "end": v(19.03, -8.19) * mm});
            skLineSegment(sketch, "E320.MirrorCS", {"start": v(13.56, -23.73) * mm, "end": v(10.88, -17.97) * mm});
            skArc(sketch, "E321.MirrorCS", {"start": v(-47.96, -12.47) * mm, "mid": v(-48.12, -12.78) * mm, "end": v(-48.05, -13.12) * mm});
            skLineSegment(sketch, "E322.MirrorCS", {"start": v(10.2, -17.79) * mm, "end": v(6.65, -20.27) * mm});
            skLineSegment(sketch, "E323.MirrorCS", {"start": v(6.59, -20.98) * mm, "end": v(11.08, -25.47) * mm});
            skLineSegment(sketch, "E324.MirrorCS", {"start": v(-11.15, -26.17) * mm, "end": v(-9.51, -32.3) * mm});
            skArc(sketch, "E325.MirrorCS", {"start": v(-13.1, -26.17) * mm, "mid": v(-13.16, -25.78) * mm, "end": v(-13.5, -25.59) * mm});
            skLineSegment(sketch, "E326.MirrorCS", {"start": v(-17.56, -25.23) * mm, "end": v(-13.5, -25.59) * mm});
            skLineSegment(sketch, "E327.MirrorCS", {"start": v(-13.1, -26.17) * mm, "end": v(-14.74, -32.3) * mm});
            skLineSegment(sketch, "E328.MirrorCS", {"start": v(16.22, -12.6) * mm, "end": v(22.08, -15.03) * mm});
            skArc(sketch, "E329.MirrorCS", {"start": v(18.32, -8.28) * mm, "mid": v(18.65, -8.07) * mm, "end": v(19.03, -8.19) * mm});
            skLineSegment(sketch, "E330.MirrorCS", {"start": v(18.32, -8.28) * mm, "end": v(16, -11.93) * mm});
            skLineSegment(sketch, "E331.MirrorCS", {"start": v(-24.9, -30.43) * mm, "end": v(-24.12, -24.13) * mm});
            skLineSegment(sketch, "E332.MirrorCS", {"start": v(-6.7, -25.23) * mm, "end": v(-10.75, -25.59) * mm});
            skArc(sketch, "E333.MirrorCS", {"start": v(-11.15, -26.17) * mm, "mid": v(-11.09, -25.78) * mm, "end": v(-10.75, -25.59) * mm});
            skLineSegment(sketch, "E334.MirrorCS", {"start": v(-53.98, 7.69) * mm, "end": v(-48.1, 9.26) * mm});
            skArc(sketch, "E335.MirrorCS", {"start": v(-47.24, 8.67) * mm, "mid": v(-47.53, 9.16) * mm, "end": v(-48.1, 9.26) * mm});
            skLineSegment(sketch, "E336.MirrorCS", {"start": v(-47.96, -12.47) * mm, "end": v(-43.28, -8.19) * mm});
            skPoint(sketch, "E337.MirrorP", {"position": v(-53.48, 0.6) * mm});
            skPoint(sketch, "E338.MirrorP", {"position": v(-46.84, 3.71) * mm});
            skPoint(sketch, "E339.MirrorP", {"position": v(1, -29.67) * mm});
            skPoint(sketch, "E340.MirrorP", {"position": v(-9.4, -32.71) * mm});
            skPoint(sketch, "E341.MirrorP", {"position": v(-54.4, 7.58) * mm});
            skPoint(sketch, "E342.MirrorP", {"position": v(-18.1, -25.18) * mm});
            skPoint(sketch, "E343.MirrorP", {"position": v(29.23, 0.6) * mm});
            skPoint(sketch, "E344.MirrorP", {"position": v(30.14, 7.58) * mm});
            skPoint(sketch, "E345.MirrorP", {"position": v(-12.95, -25.63) * mm});
            skPoint(sketch, "E346.MirrorP", {"position": v(-6.78, -32.48) * mm});
            skPoint(sketch, "E347.MirrorP", {"position": v(-17.47, -32.48) * mm});
            skPoint(sketch, "E348.MirrorP", {"position": v(-5.14, -25.1) * mm});
            skPoint(sketch, "E349.MirrorP", {"position": v(10.64, -17.47) * mm});
            skPoint(sketch, "E350.MirrorP", {"position": v(-38, -24.11) * mm});
            skPoint(sketch, "E351.MirrorP", {"position": v(24.03, -12.76) * mm});
            skPoint(sketch, "E352.MirrorP", {"position": v(27.35, -6.34) * mm});
            skPoint(sketch, "E353.MirrorP", {"position": v(22.6, 4.06) * mm});
            skPoint(sketch, "E354.MirrorP", {"position": v(-51.6, -6.34) * mm});
            skPoint(sketch, "E355.MirrorP", {"position": v(7.48, -28.03) * mm});
            skPoint(sketch, "E356.MirrorP", {"position": v(13.74, -24.11) * mm});
            skPoint(sketch, "E357.MirrorP", {"position": v(-6.15, -25.18) * mm});
            skPoint(sketch, "E358.MirrorP", {"position": v(-31.73, -28.03) * mm});
            skPoint(sketch, "E359.MirrorP", {"position": v(-48.28, -12.76) * mm});
            skPoint(sketch, "E360.MirrorP", {"position": v(19.27, -19.05) * mm});
            skPoint(sketch, "E361.MirrorP", {"position": v(-43.52, -19.05) * mm});
            skPoint(sketch, "E362.MirrorP", {"position": v(-25.24, -29.67) * mm});
            skPoint(sketch, "E363.MirrorP", {"position": v(-35.47, -16.9) * mm});
            skPoint(sketch, "E364.MirrorP", {"position": v(-29.17, -29.36) * mm});
            skPoint(sketch, "E365.MirrorP", {"position": v(6.2, -20.58) * mm});
            skPoint(sketch, "E366.MirrorP", {"position": v(18.62, -7.81) * mm});
            skPoint(sketch, "E367.MirrorP", {"position": v(28.48, -2.18) * mm});
            skPoint(sketch, "E368.MirrorP", {"position": v(-35.63, -25.77) * mm});
            skPoint(sketch, "E369.MirrorP", {"position": v(-30.45, -20.58) * mm});
            skPoint(sketch, "E370.MirrorP", {"position": v(-45.43, -1.53) * mm});
            skPoint(sketch, "E371.MirrorP", {"position": v(-52.73, -2.18) * mm});
            skPoint(sketch, "E372.MirrorP", {"position": v(4.92, -29.36) * mm});
            skPoint(sketch, "E373.MirrorP", {"position": v(-24.05, -23.58) * mm});
            skPoint(sketch, "E374.MirrorP", {"position": v(22.48, -15.2) * mm});
            skPoint(sketch, "E375.MirrorP", {"position": v(-41.48, -21.1) * mm});
            skPoint(sketch, "E376.MirrorP", {"position": v(-43.3, -7.06) * mm});
            skPoint(sketch, "E377.MirrorP", {"position": v(-14.85, -32.71) * mm});
            skPoint(sketch, "E378.MirrorP", {"position": v(15.7, -12.4) * mm});
            skPoint(sketch, "E379.MirrorP", {"position": v(22.6, 3.71) * mm});
            skPoint(sketch, "E380.MirrorP", {"position": v(-29.54, -21.04) * mm});
            skPoint(sketch, "E381.MirrorP", {"position": v(-47.31, 9.47) * mm});
            skPoint(sketch, "E382.MirrorP", {"position": v(-0.2, -23.58) * mm});
            skPoint(sketch, "E383.MirrorP", {"position": v(-46.84, 4.06) * mm});
            skPoint(sketch, "E384.MirrorP", {"position": v(11.38, -25.77) * mm});
            skPoint(sketch, "E385.MirrorP", {"position": v(-39.96, -12.4) * mm});
            skPoint(sketch, "E386.MirrorP", {"position": v(0.47, -23.54) * mm});
            skPoint(sketch, "E387.MirrorP", {"position": v(-42.87, -7.81) * mm});
            skPoint(sketch, "E388.MirrorP", {"position": v(-45.6, -2.14) * mm});
            skPoint(sketch, "E389.MirrorP", {"position": v(19.06, -7.06) * mm});
            skPoint(sketch, "E390.MirrorP", {"position": v(-22.45, -31.63) * mm});
            skPoint(sketch, "E391.MirrorP", {"position": v(29.9, 4.7) * mm});
            skPoint(sketch, "E392.MirrorP", {"position": v(-50.39, -8.95) * mm});
            skPoint(sketch, "E393.MirrorP", {"position": v(-39.3, -13.06) * mm});
            skPoint(sketch, "E394.MirrorP", {"position": v(15.05, -13.06) * mm});
            skPoint(sketch, "E395.MirrorP", {"position": v(21.18, -1.53) * mm});
            skPoint(sketch, "E396.MirrorP", {"position": v(-24.72, -23.54) * mm});
            skPoint(sketch, "E397.MirrorP", {"position": v(-19.1, -25.1) * mm});
            skPoint(sketch, "E398.MirrorP", {"position": v(23.06, 9.47) * mm});
            skPoint(sketch, "E399.MirrorP", {"position": v(11.22, -16.9) * mm});
            skPoint(sketch, "E400.MirrorP", {"position": v(21.35, -2.14) * mm});
            skPoint(sketch, "E401.MirrorP", {"position": v(-1.8, -31.63) * mm});
            skPoint(sketch, "E402.MirrorP", {"position": v(26.14, -8.95) * mm});
            skPoint(sketch, "E403.MirrorP", {"position": v(-11.3, -25.63) * mm});
            skPoint(sketch, "E404.MirrorP", {"position": v(-46.73, -15.2) * mm});
            skPoint(sketch, "E405.MirrorP", {"position": v(17.23, -21.1) * mm});
            skPoint(sketch, "E406.MirrorP", {"position": v(5.29, -21.04) * mm});
            skPoint(sketch, "E407.MirrorP", {"position": v(-54.14, 4.7) * mm});
            skPoint(sketch, "E408.MirrorP", {"position": v(-34.9, -17.47) * mm});
            skSolve(sketch);
        }
        {
            var Q0;
            Q0=qCreatedBy(makeId("Front.planeOp"),FACE);
            var sketch = newSketch(context, id + "F1", { "sketchPlane" : qUnion([Q0])});
            skCircle(sketch, "E409", {"center": v(44.86, -37.08) * mm, "radius": 19.05 * mm});
            skCircle(sketch, "E410", {"center": v(44.86, -37.08) * mm, "radius": 6.35 * mm});
            skLineSegment(sketch, "E411", {"start": v(45.77, -19.67) * mm, "end": v(46.98, -15.17) * mm});
            skLineSegment(sketch, "E412", {"start": v(49.3, -19.98) * mm, "end": v(48.9, -15.34) * mm});
            skLineSegment(sketch, "E413", {"start": v(48.86, -14.92) * mm, "end": v(47.09, -14.76) * mm});
            skLineSegment(sketch, "E414", {"start": v(45.77, -19.67) * mm, "end": v(49.3, -19.98) * mm});
            skLineSegment(sketch, "E415.0", {"start": v(47.51, -14.8) * mm, "end": v(48.43, -14.88) * mm, "construction": true});
            skLineSegment(sketch, "E416.0", {"start": v(45.77, -19.67) * mm, "end": v(49.3, -19.98) * mm, "construction": true});
            skLineSegment(sketch, "E417", {"start": v(51.2, -20.7) * mm, "end": v(54.15, -16.84) * mm});
            skLineSegment(sketch, "E418", {"start": v(54.34, -22.33) * mm, "end": v(56.01, -17.84) * mm});
            skLineSegment(sketch, "E419", {"start": v(56.17, -17.42) * mm, "end": v(54.41, -16.5) * mm});
            skLineSegment(sketch, "E420", {"start": v(51.2, -20.7) * mm, "end": v(54.34, -22.33) * mm});
            skLineSegment(sketch, "E421.0", {"start": v(54.8, -16.7) * mm, "end": v(55.77, -17.2) * mm});
            skLineSegment(sketch, "E422.0", {"start": v(51.2, -20.7) * mm, "end": v(54.34, -22.33) * mm, "construction": true});
            skLineSegment(sketch, "E423", {"start": v(56.05, -23.57) * mm, "end": v(59.87, -20.9) * mm});
            skLineSegment(sketch, "E424", {"start": v(58.56, -26.08) * mm, "end": v(61.23, -22.27) * mm});
            skLineSegment(sketch, "E425", {"start": v(61.47, -21.92) * mm, "end": v(60.21, -20.66) * mm});
            skLineSegment(sketch, "E426", {"start": v(56.05, -23.57) * mm, "end": v(58.56, -26.08) * mm});
            skLineSegment(sketch, "E427.0", {"start": v(60.52, -20.96) * mm, "end": v(61.17, -21.61) * mm, "construction": true});
            skLineSegment(sketch, "E428.0", {"start": v(56.05, -23.57) * mm, "end": v(58.56, -26.08) * mm, "construction": true});
            skLineSegment(sketch, "E429", {"start": v(59.78, -27.97) * mm, "end": v(64.27, -26.74) * mm});
            skLineSegment(sketch, "E430", {"start": v(61.3, -31.17) * mm, "end": v(65.1, -28.48) * mm});
            skLineSegment(sketch, "E431", {"start": v(65.44, -28.24) * mm, "end": v(64.68, -26.63) * mm});
            skLineSegment(sketch, "E432", {"start": v(59.78, -27.97) * mm, "end": v(61.3, -31.17) * mm});
            skLineSegment(sketch, "E433.0", {"start": v(64.86, -27.02) * mm, "end": v(65.26, -27.85) * mm, "construction": true});
            skLineSegment(sketch, "E434.0", {"start": v(59.78, -27.97) * mm, "end": v(61.3, -31.17) * mm, "construction": true});
            skLineSegment(sketch, "E435", {"start": v(61.8, -32.6) * mm, "end": v(66.46, -32.6) * mm});
            skLineSegment(sketch, "E436", {"start": v(62.42, -36.1) * mm, "end": v(66.8, -34.5) * mm});
            skLineSegment(sketch, "E437", {"start": v(67.2, -34.35) * mm, "end": v(66.89, -32.6) * mm});
            skLineSegment(sketch, "E438", {"start": v(61.8, -32.6) * mm, "end": v(62.42, -36.1) * mm});
            skLineSegment(sketch, "E439.0", {"start": v(66.96, -33.02) * mm, "end": v(67.12, -33.93) * mm, "construction": true});
            skLineSegment(sketch, "E440.0", {"start": v(61.8, -32.6) * mm, "end": v(62.42, -36.1) * mm, "construction": true});
            skLineSegment(sketch, "E441.MirrorCS", {"start": v(24.29, -28.24) * mm, "end": v(25.05, -26.63) * mm});
            skLineSegment(sketch, "E442.MirrorCS", {"start": v(28.26, -21.92) * mm, "end": v(29.51, -20.66) * mm});
            skLineSegment(sketch, "E443.MirrorCS", {"start": v(22.53, -34.35) * mm, "end": v(22.84, -32.6) * mm});
            skLineSegment(sketch, "E444.MirrorCS", {"start": v(40.87, -14.92) * mm, "end": v(42.71, -14.76) * mm});
            skLineSegment(sketch, "E445.MirrorCS", {"start": v(33.86, -17.48) * mm, "end": v(35.43, -16.66) * mm});
            skLineSegment(sketch, "E446.MirrorCS", {"start": v(22.77, -33.02) * mm, "end": v(22.6, -33.93) * mm, "construction": true});
            skLineSegment(sketch, "E447.MirrorCS", {"start": v(29.21, -20.96) * mm, "end": v(28.56, -21.61) * mm, "construction": true});
            skLineSegment(sketch, "E448.MirrorCS", {"start": v(35.06, -16.86) * mm, "end": v(34.24, -17.29) * mm, "construction": true});
            skLineSegment(sketch, "E449.MirrorCS", {"start": v(42.29, -14.8) * mm, "end": v(41.3, -14.88) * mm, "construction": true});
            skLineSegment(sketch, "E450.MirrorCS", {"start": v(24.86, -27.02) * mm, "end": v(24.47, -27.85) * mm, "construction": true});
            skLineSegment(sketch, "E451.MirrorCS", {"start": v(44.04, -19.73) * mm, "end": v(40.43, -19.98) * mm});
            skLineSegment(sketch, "E452.MirrorCS", {"start": v(38.53, -20.7) * mm, "end": v(35.39, -22.33) * mm});
            skLineSegment(sketch, "E453.MirrorCS", {"start": v(27.92, -32.6) * mm, "end": v(27.3, -36.1) * mm});
            skLineSegment(sketch, "E454.MirrorCS", {"start": v(33.67, -23.57) * mm, "end": v(31.17, -26.08) * mm});
            skLineSegment(sketch, "E455.MirrorCS", {"start": v(29.95, -27.97) * mm, "end": v(28.43, -31.17) * mm});
            skLineSegment(sketch, "E456.MirrorCS", {"start": v(38.53, -20.7) * mm, "end": v(35.7, -17) * mm});
            skLineSegment(sketch, "E457.MirrorCS", {"start": v(27.92, -32.6) * mm, "end": v(27.3, -36.1) * mm, "construction": true});
            skLineSegment(sketch, "E458.MirrorCS", {"start": v(44.04, -19.73) * mm, "end": v(42.82, -15.17) * mm});
            skLineSegment(sketch, "E459.MirrorCS", {"start": v(38.53, -20.7) * mm, "end": v(35.39, -22.33) * mm, "construction": true});
            skLineSegment(sketch, "E460.MirrorCS", {"start": v(27.92, -32.6) * mm, "end": v(23.27, -32.6) * mm});
            skLineSegment(sketch, "E461.MirrorCS", {"start": v(44.04, -19.73) * mm, "end": v(40.43, -19.98) * mm, "construction": true});
            skLineSegment(sketch, "E462.MirrorCS", {"start": v(33.67, -23.57) * mm, "end": v(29.86, -20.9) * mm});
            skLineSegment(sketch, "E463.MirrorCS", {"start": v(28.43, -31.17) * mm, "end": v(24.63, -28.48) * mm});
            skLineSegment(sketch, "E464.MirrorCS", {"start": v(33.67, -23.57) * mm, "end": v(31.17, -26.08) * mm, "construction": true});
            skLineSegment(sketch, "E465.MirrorCS", {"start": v(29.95, -27.97) * mm, "end": v(28.43, -31.17) * mm, "construction": true});
            skLineSegment(sketch, "E466.MirrorCS", {"start": v(29.95, -27.97) * mm, "end": v(25.46, -26.74) * mm});
            skLineSegment(sketch, "E467.MirrorCS", {"start": v(27.3, -36.1) * mm, "end": v(22.93, -34.5) * mm});
            skLineSegment(sketch, "E468.MirrorCS", {"start": v(31.17, -26.08) * mm, "end": v(28.5, -22.27) * mm});
            skLineSegment(sketch, "E469.MirrorCS", {"start": v(40.43, -19.98) * mm, "end": v(40.83, -15.34) * mm});
            skLineSegment(sketch, "E470.MirrorCS", {"start": v(35.39, -22.33) * mm, "end": v(33.99, -17.89) * mm});
            skLineSegment(sketch, "E471.MirrorCS", {"start": v(48.86, -59.25) * mm, "end": v(47.09, -59.4) * mm});
            skLineSegment(sketch, "E472.MirrorCS", {"start": v(61.47, -52.25) * mm, "end": v(60.21, -53.5) * mm});
            skLineSegment(sketch, "E473.MirrorCS", {"start": v(24.29, -45.93) * mm, "end": v(25.05, -47.54) * mm});
            skLineSegment(sketch, "E474.MirrorCS", {"start": v(65.44, -45.93) * mm, "end": v(64.68, -47.54) * mm});
            skLineSegment(sketch, "E475.MirrorCS", {"start": v(28.26, -52.25) * mm, "end": v(29.51, -53.5) * mm});
            skLineSegment(sketch, "E476.MirrorCS", {"start": v(33.86, -56.69) * mm, "end": v(35.43, -57.5) * mm});
            skLineSegment(sketch, "E477.MirrorCS", {"start": v(55.87, -56.69) * mm, "end": v(54.3, -57.5) * mm});
            skLineSegment(sketch, "E478.MirrorCS", {"start": v(67.2, -39.81) * mm, "end": v(66.89, -41.57) * mm});
            skLineSegment(sketch, "E479.MirrorCS", {"start": v(40.87, -59.25) * mm, "end": v(42.64, -59.4) * mm});
            skLineSegment(sketch, "E480.MirrorCS", {"start": v(22.53, -39.81) * mm, "end": v(22.84, -41.57) * mm});
            skLineSegment(sketch, "E481.MirrorCS", {"start": v(60.52, -53.2) * mm, "end": v(61.17, -52.55) * mm, "construction": true});
            skLineSegment(sketch, "E482.MirrorCS", {"start": v(42.22, -59.37) * mm, "end": v(41.3, -59.29) * mm, "construction": true});
            skLineSegment(sketch, "E483.MirrorCS", {"start": v(24.86, -47.15) * mm, "end": v(24.47, -46.32) * mm, "construction": true});
            skLineSegment(sketch, "E484.MirrorCS", {"start": v(47.51, -59.37) * mm, "end": v(48.43, -59.29) * mm, "construction": true});
            skLineSegment(sketch, "E485.MirrorCS", {"start": v(29.21, -53.2) * mm, "end": v(28.56, -52.55) * mm, "construction": true});
            skLineSegment(sketch, "E486.MirrorCS", {"start": v(54.67, -57.3) * mm, "end": v(55.5, -56.88) * mm, "construction": true});
            skLineSegment(sketch, "E487.MirrorCS", {"start": v(35.06, -57.3) * mm, "end": v(34.24, -56.88) * mm, "construction": true});
            skLineSegment(sketch, "E488.MirrorCS", {"start": v(64.86, -47.15) * mm, "end": v(65.26, -46.32) * mm, "construction": true});
            skLineSegment(sketch, "E489.MirrorCS", {"start": v(66.96, -41.15) * mm, "end": v(67.12, -40.23) * mm, "construction": true});
            skLineSegment(sketch, "E490.MirrorCS", {"start": v(22.77, -41.15) * mm, "end": v(22.6, -40.23) * mm, "construction": true});
            skLineSegment(sketch, "E491.MirrorCS", {"start": v(33.67, -50.6) * mm, "end": v(31.17, -48.1) * mm});
            skLineSegment(sketch, "E492.MirrorCS", {"start": v(59.78, -46.2) * mm, "end": v(61.3, -43) * mm});
            skLineSegment(sketch, "E493.MirrorCS", {"start": v(45.77, -54.5) * mm, "end": v(49.3, -54.2) * mm});
            skLineSegment(sketch, "E494.MirrorCS", {"start": v(61.8, -41.57) * mm, "end": v(62.42, -38.08) * mm});
            skLineSegment(sketch, "E495.MirrorCS", {"start": v(51.2, -53.48) * mm, "end": v(54.34, -51.84) * mm});
            skLineSegment(sketch, "E496.MirrorCS", {"start": v(27.92, -41.57) * mm, "end": v(27.3, -38.08) * mm});
            skLineSegment(sketch, "E497.MirrorCS", {"start": v(29.95, -46.2) * mm, "end": v(28.43, -43) * mm});
            skLineSegment(sketch, "E498.MirrorCS", {"start": v(38.53, -53.48) * mm, "end": v(35.39, -51.84) * mm});
            skLineSegment(sketch, "E499.MirrorCS", {"start": v(56.05, -50.6) * mm, "end": v(58.56, -48.1) * mm});
            skLineSegment(sketch, "E500.MirrorCS", {"start": v(43.96, -54.5) * mm, "end": v(40.43, -54.2) * mm});
            skLineSegment(sketch, "E501.MirrorCS", {"start": v(59.78, -46.2) * mm, "end": v(61.3, -43) * mm, "construction": true});
            skLineSegment(sketch, "E502.MirrorCS", {"start": v(62.42, -38.08) * mm, "end": v(66.8, -39.67) * mm});
            skLineSegment(sketch, "E503.MirrorCS", {"start": v(59.78, -46.2) * mm, "end": v(64.27, -47.43) * mm});
            skLineSegment(sketch, "E504.MirrorCS", {"start": v(45.77, -54.5) * mm, "end": v(46.98, -59) * mm});
            skLineSegment(sketch, "E505.MirrorCS", {"start": v(38.53, -53.48) * mm, "end": v(35.7, -57.17) * mm});
            skLineSegment(sketch, "E506.MirrorCS", {"start": v(58.56, -48.1) * mm, "end": v(61.23, -51.9) * mm});
            skLineSegment(sketch, "E507.MirrorCS", {"start": v(40.43, -54.2) * mm, "end": v(40.83, -58.83) * mm});
            skLineSegment(sketch, "E508.MirrorCS", {"start": v(29.95, -46.2) * mm, "end": v(28.43, -43) * mm, "construction": true});
            skLineSegment(sketch, "E509.MirrorCS", {"start": v(43.96, -54.5) * mm, "end": v(42.75, -59) * mm});
            skLineSegment(sketch, "E510.MirrorCS", {"start": v(56.05, -50.6) * mm, "end": v(59.87, -53.26) * mm});
            skLineSegment(sketch, "E511.MirrorCS", {"start": v(49.3, -54.2) * mm, "end": v(48.9, -58.83) * mm});
            skLineSegment(sketch, "E512.MirrorCS", {"start": v(29.95, -46.2) * mm, "end": v(25.46, -47.43) * mm});
            skLineSegment(sketch, "E513.MirrorCS", {"start": v(54.34, -51.84) * mm, "end": v(55.74, -56.28) * mm});
            skLineSegment(sketch, "E514.MirrorCS", {"start": v(51.2, -53.48) * mm, "end": v(54.03, -57.17) * mm});
            skLineSegment(sketch, "E515.MirrorCS", {"start": v(38.53, -53.48) * mm, "end": v(35.39, -51.84) * mm, "construction": true});
            skLineSegment(sketch, "E516.MirrorCS", {"start": v(45.77, -54.5) * mm, "end": v(49.3, -54.2) * mm, "construction": true});
            skLineSegment(sketch, "E517.MirrorCS", {"start": v(33.67, -50.6) * mm, "end": v(29.86, -53.26) * mm});
            skLineSegment(sketch, "E518.MirrorCS", {"start": v(61.8, -41.57) * mm, "end": v(66.46, -41.57) * mm});
            skLineSegment(sketch, "E519.MirrorCS", {"start": v(56.05, -50.6) * mm, "end": v(58.56, -48.1) * mm, "construction": true});
            skLineSegment(sketch, "E520.MirrorCS", {"start": v(43.96, -54.5) * mm, "end": v(40.43, -54.2) * mm, "construction": true});
            skLineSegment(sketch, "E521.MirrorCS", {"start": v(31.17, -48.1) * mm, "end": v(28.5, -51.9) * mm});
            skLineSegment(sketch, "E522.MirrorCS", {"start": v(28.43, -43) * mm, "end": v(24.63, -45.68) * mm});
            skLineSegment(sketch, "E523.MirrorCS", {"start": v(51.2, -53.48) * mm, "end": v(54.34, -51.84) * mm, "construction": true});
            skLineSegment(sketch, "E524.MirrorCS", {"start": v(61.3, -43) * mm, "end": v(65.1, -45.68) * mm});
            skLineSegment(sketch, "E525.MirrorCS", {"start": v(33.67, -50.6) * mm, "end": v(31.17, -48.1) * mm, "construction": true});
            skLineSegment(sketch, "E526.MirrorCS", {"start": v(27.92, -41.57) * mm, "end": v(27.3, -38.08) * mm, "construction": true});
            skLineSegment(sketch, "E527.MirrorCS", {"start": v(61.8, -41.57) * mm, "end": v(62.42, -38.08) * mm, "construction": true});
            skLineSegment(sketch, "E528.MirrorCS", {"start": v(27.3, -38.08) * mm, "end": v(22.93, -39.67) * mm});
            skLineSegment(sketch, "E529.MirrorCS", {"start": v(27.92, -41.57) * mm, "end": v(23.27, -41.57) * mm});
            skLineSegment(sketch, "E530.MirrorCS", {"start": v(35.39, -51.84) * mm, "end": v(33.99, -56.28) * mm});
            skPoint(sketch, "E531.visualSharp", {"position": v(42.71, -14.76) * mm});
            skArc(sketch, "E531.filletArc", {"start": v(42.82, -15.17) * mm, "mid": v(42.62, -14.88) * mm, "end": v(42.29, -14.8) * mm});
            skPoint(sketch, "E532.visualSharp", {"position": v(40.87, -14.92) * mm});
            skArc(sketch, "E532.filletArc", {"start": v(41.3, -14.88) * mm, "mid": v(40.98, -15.03) * mm, "end": v(40.83, -15.34) * mm});
            skPoint(sketch, "E533.visualSharp", {"position": v(47.09, -14.76) * mm});
            skArc(sketch, "E533.filletArc", {"start": v(47.51, -14.8) * mm, "mid": v(47.18, -14.89) * mm, "end": v(46.98, -15.17) * mm});
            skPoint(sketch, "E534.visualSharp", {"position": v(48.86, -14.92) * mm});
            skArc(sketch, "E534.filletArc", {"start": v(48.9, -15.34) * mm, "mid": v(48.75, -15.03) * mm, "end": v(48.43, -14.88) * mm});
            skPoint(sketch, "E535.visualSharp", {"position": v(54.41, -16.5) * mm});
            skArc(sketch, "E535.filletArc", {"start": v(54.8, -16.7) * mm, "mid": v(54.45, -16.65) * mm, "end": v(54.15, -16.84) * mm});
            skPoint(sketch, "E536.visualSharp", {"position": v(56.17, -17.42) * mm});
            skArc(sketch, "E536.filletArc", {"start": v(56.01, -17.84) * mm, "mid": v(56.01, -17.48) * mm, "end": v(55.77, -17.2) * mm});
            skPoint(sketch, "E537.visualSharp", {"position": v(60.21, -20.66) * mm});
            skArc(sketch, "E537.filletArc", {"start": v(60.52, -20.96) * mm, "mid": v(60.2, -20.81) * mm, "end": v(59.87, -20.9) * mm});
            skPoint(sketch, "E538.visualSharp", {"position": v(61.47, -21.92) * mm});
            skArc(sketch, "E538.filletArc", {"start": v(61.23, -22.27) * mm, "mid": v(61.32, -21.93) * mm, "end": v(61.17, -21.61) * mm});
            skPoint(sketch, "E539.visualSharp", {"position": v(64.68, -26.63) * mm});
            skArc(sketch, "E539.filletArc", {"start": v(64.86, -27.02) * mm, "mid": v(64.62, -26.77) * mm, "end": v(64.27, -26.74) * mm});
            skPoint(sketch, "E540.visualSharp", {"position": v(65.44, -28.24) * mm});
            skArc(sketch, "E540.filletArc", {"start": v(65.1, -28.48) * mm, "mid": v(65.3, -28.2) * mm, "end": v(65.26, -27.85) * mm});
            skPoint(sketch, "E541.visualSharp", {"position": v(66.89, -32.6) * mm});
            skArc(sketch, "E541.filletArc", {"start": v(66.96, -33.02) * mm, "mid": v(66.79, -32.72) * mm, "end": v(66.46, -32.6) * mm});
            skPoint(sketch, "E542.visualSharp", {"position": v(67.2, -34.35) * mm});
            skArc(sketch, "E542.filletArc", {"start": v(66.8, -34.5) * mm, "mid": v(67.06, -34.28) * mm, "end": v(67.12, -33.93) * mm});
            skPoint(sketch, "E543.visualSharp", {"position": v(67.2, -39.81) * mm});
            skArc(sketch, "E543.filletArc", {"start": v(67.12, -40.23) * mm, "mid": v(67.06, -39.9) * mm, "end": v(66.8, -39.67) * mm});
            skPoint(sketch, "E544.visualSharp", {"position": v(66.89, -41.57) * mm});
            skArc(sketch, "E544.filletArc", {"start": v(66.46, -41.57) * mm, "mid": v(66.79, -41.45) * mm, "end": v(66.96, -41.15) * mm});
            skPoint(sketch, "E545.visualSharp", {"position": v(65.44, -45.93) * mm});
            skArc(sketch, "E545.filletArc", {"start": v(65.26, -46.32) * mm, "mid": v(65.3, -45.97) * mm, "end": v(65.1, -45.68) * mm});
            skPoint(sketch, "E546.visualSharp", {"position": v(64.68, -47.54) * mm});
            skArc(sketch, "E546.filletArc", {"start": v(64.27, -47.43) * mm, "mid": v(64.62, -47.4) * mm, "end": v(64.86, -47.15) * mm});
            skPoint(sketch, "E547.visualSharp", {"position": v(61.47, -52.25) * mm});
            skArc(sketch, "E547.filletArc", {"start": v(61.17, -52.55) * mm, "mid": v(61.32, -52.24) * mm, "end": v(61.23, -51.9) * mm});
            skPoint(sketch, "E548.visualSharp", {"position": v(60.21, -53.5) * mm});
            skArc(sketch, "E548.filletArc", {"start": v(59.87, -53.26) * mm, "mid": v(60.2, -53.35) * mm, "end": v(60.52, -53.2) * mm});
            skPoint(sketch, "E549.visualSharp", {"position": v(55.87, -56.69) * mm});
            skArc(sketch, "E549.filletArc", {"start": v(55.5, -56.88) * mm, "mid": v(55.73, -56.63) * mm, "end": v(55.74, -56.28) * mm});
            skPoint(sketch, "E550.visualSharp", {"position": v(54.3, -57.5) * mm});
            skArc(sketch, "E550.filletArc", {"start": v(54.03, -57.17) * mm, "mid": v(54.33, -57.36) * mm, "end": v(54.67, -57.3) * mm});
            skPoint(sketch, "E551.visualSharp", {"position": v(48.86, -59.25) * mm});
            skArc(sketch, "E551.filletArc", {"start": v(48.43, -59.29) * mm, "mid": v(48.75, -59.14) * mm, "end": v(48.9, -58.83) * mm});
            skPoint(sketch, "E552.visualSharp", {"position": v(47.09, -59.4) * mm});
            skArc(sketch, "E552.filletArc", {"start": v(46.98, -59) * mm, "mid": v(47.18, -59.28) * mm, "end": v(47.51, -59.37) * mm});
            skPoint(sketch, "E553.visualSharp", {"position": v(42.64, -59.4) * mm});
            skArc(sketch, "E553.filletArc", {"start": v(42.22, -59.37) * mm, "mid": v(42.55, -59.28) * mm, "end": v(42.75, -59) * mm});
            skPoint(sketch, "E554.visualSharp", {"position": v(40.87, -59.25) * mm});
            skArc(sketch, "E554.filletArc", {"start": v(40.83, -58.83) * mm, "mid": v(40.98, -59.14) * mm, "end": v(41.3, -59.29) * mm});
            skPoint(sketch, "E555.visualSharp", {"position": v(35.43, -57.5) * mm});
            skArc(sketch, "E555.filletArc", {"start": v(35.06, -57.3) * mm, "mid": v(35.4, -57.36) * mm, "end": v(35.7, -57.17) * mm});
            skPoint(sketch, "E556.visualSharp", {"position": v(33.86, -56.69) * mm});
            skArc(sketch, "E556.filletArc", {"start": v(33.99, -56.28) * mm, "mid": v(34, -56.63) * mm, "end": v(34.24, -56.88) * mm});
            skPoint(sketch, "E557.visualSharp", {"position": v(29.51, -53.5) * mm});
            skArc(sketch, "E557.filletArc", {"start": v(29.21, -53.2) * mm, "mid": v(29.53, -53.35) * mm, "end": v(29.86, -53.26) * mm});
            skPoint(sketch, "E558.visualSharp", {"position": v(28.26, -52.25) * mm});
            skArc(sketch, "E558.filletArc", {"start": v(28.5, -51.9) * mm, "mid": v(28.4, -52.24) * mm, "end": v(28.56, -52.55) * mm});
            skPoint(sketch, "E559.visualSharp", {"position": v(25.05, -47.54) * mm});
            skArc(sketch, "E559.filletArc", {"start": v(24.86, -47.15) * mm, "mid": v(25.11, -47.4) * mm, "end": v(25.46, -47.43) * mm});
            skPoint(sketch, "E560.visualSharp", {"position": v(24.29, -45.93) * mm});
            skArc(sketch, "E560.filletArc", {"start": v(24.63, -45.68) * mm, "mid": v(24.44, -45.97) * mm, "end": v(24.47, -46.32) * mm});
            skPoint(sketch, "E561.visualSharp", {"position": v(22.84, -41.57) * mm});
            skArc(sketch, "E561.filletArc", {"start": v(22.77, -41.15) * mm, "mid": v(22.94, -41.45) * mm, "end": v(23.27, -41.57) * mm});
            skPoint(sketch, "E562.visualSharp", {"position": v(22.53, -39.81) * mm});
            skArc(sketch, "E562.filletArc", {"start": v(22.93, -39.67) * mm, "mid": v(22.67, -39.9) * mm, "end": v(22.6, -40.23) * mm});
            skPoint(sketch, "E563.visualSharp", {"position": v(22.53, -34.35) * mm});
            skArc(sketch, "E563.filletArc", {"start": v(22.6, -33.93) * mm, "mid": v(22.67, -34.28) * mm, "end": v(22.93, -34.5) * mm});
            skPoint(sketch, "E564.visualSharp", {"position": v(22.84, -32.6) * mm});
            skArc(sketch, "E564.filletArc", {"start": v(23.27, -32.6) * mm, "mid": v(22.94, -32.72) * mm, "end": v(22.77, -33.02) * mm});
            skPoint(sketch, "E565.visualSharp", {"position": v(24.29, -28.24) * mm});
            skArc(sketch, "E565.filletArc", {"start": v(24.47, -27.85) * mm, "mid": v(24.44, -28.2) * mm, "end": v(24.63, -28.48) * mm});
            skPoint(sketch, "E566.visualSharp", {"position": v(25.05, -26.63) * mm});
            skArc(sketch, "E566.filletArc", {"start": v(25.46, -26.74) * mm, "mid": v(25.11, -26.77) * mm, "end": v(24.86, -27.02) * mm});
            skPoint(sketch, "E567.visualSharp", {"position": v(28.26, -21.92) * mm});
            skArc(sketch, "E567.filletArc", {"start": v(28.56, -21.61) * mm, "mid": v(28.4, -21.93) * mm, "end": v(28.5, -22.27) * mm});
            skPoint(sketch, "E568.visualSharp", {"position": v(29.51, -20.66) * mm});
            skArc(sketch, "E568.filletArc", {"start": v(29.86, -20.9) * mm, "mid": v(29.53, -20.81) * mm, "end": v(29.21, -20.96) * mm});
            skPoint(sketch, "E569.visualSharp", {"position": v(33.86, -17.48) * mm});
            skArc(sketch, "E569.filletArc", {"start": v(34.24, -17.29) * mm, "mid": v(34, -17.54) * mm, "end": v(33.99, -17.89) * mm});
            skPoint(sketch, "E570.visualSharp", {"position": v(35.43, -16.66) * mm});
            skArc(sketch, "E570.filletArc", {"start": v(35.7, -17) * mm, "mid": v(35.4, -16.81) * mm, "end": v(35.06, -16.86) * mm});
            skSolve(sketch);
        }
        {
            var Q0;
            Q0 = qSketchRegion(id + "F1", true);
            extrude(context, id + "F2", {"entities" : qUnion([Q0]), "depth" : 6.35 * mm});
        }
        {
            var Q0;
            Q0 = qSketchRegion(id + "F0", true);
            extrude(context, id + "F3", {"entities" : qUnion([Q0]), "depth" : 12.7 * mm});
        }
        {
            var Q0;
            Q0 = qSketchRegion(id + "F1", true);
            extrude(context, id + "F4", {"entities" : qUnion([Q0]), "depth" : 6.35 * mm});
        }
    });
